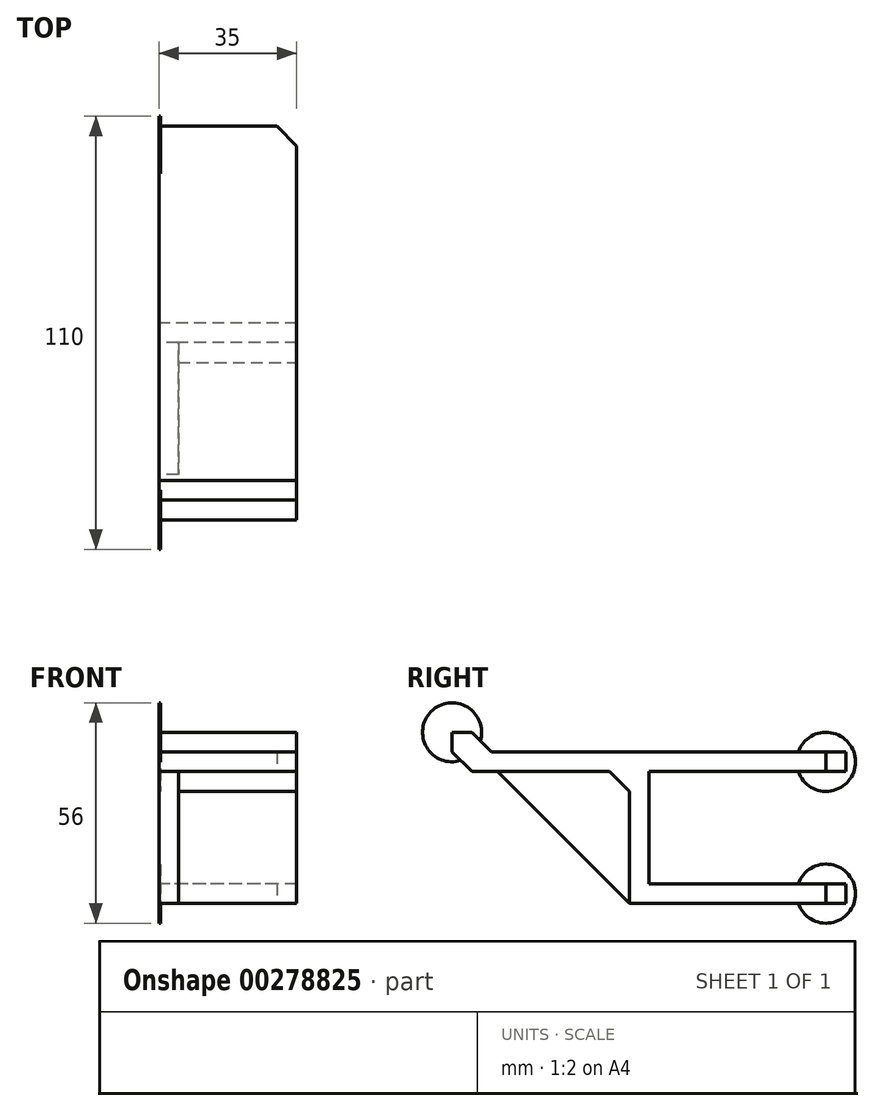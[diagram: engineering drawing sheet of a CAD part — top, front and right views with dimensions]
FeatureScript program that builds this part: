
annotation { "Feature Type Name" : "Feature", "Feature Type Description" : "" }
export const myFeature = defineFeature(function(context is Context, id is Id, definition is map)
    precondition{}
    {
        {
            var Q0;
            Q0=qCreatedBy(makeId("Right.planeOp"),FACE);
            var sketch = newSketch(context, id + "F0", { "sketchPlane" : qUnion([Q0])});
            skLineSegment(sketch, "E0.bottom", {"start": v(25, 14.25) * mm, "end": v(-25, 14.25) * mm});
            skLineSegment(sketch, "E0.top", {"start": v(25, -14.25) * mm, "end": v(-25, -14.25) * mm});
            skLineSegment(sketch, "E0.left", {"start": v(25, 14.25) * mm, "end": v(25, -14.25) * mm, "construction": true});
            skLineSegment(sketch, "E0.right", {"start": v(-25, 14.25) * mm, "end": v(-25, -14.25) * mm});
            skPoint(sketch, "E0.middle", {"position": v(0, 0) * mm});
            skLineSegment(sketch, "E1", {"start": v(25, 14.25) * mm, "end": v(25, 19.25) * mm});
            skLineSegment(sketch, "E2", {"start": v(25, 19.25) * mm, "end": v(-65, 19.25) * mm});
            skLineSegment(sketch, "E3", {"start": v(-65, 19.25) * mm, "end": v(-70, 24.25) * mm});
            skLineSegment(sketch, "E4", {"start": v(-70, 24.25) * mm, "end": v(-75, 24.25) * mm});
            skLineSegment(sketch, "E5", {"start": v(-30, -19.25) * mm, "end": v(25, -19.25) * mm});
            skLineSegment(sketch, "E6", {"start": v(25, -19.25) * mm, "end": v(25, -14.25) * mm});
            skLineSegment(sketch, "E7", {"start": v(-75, 24.25) * mm, "end": v(-75, 14.25) * mm});
            skLineSegment(sketch, "E8", {"start": v(-75, 14.25) * mm, "end": v(-30, 14.25) * mm});
            skLineSegment(sketch, "E9", {"start": v(-30, 14.25) * mm, "end": v(-30, -19.25) * mm});
            skLineSegment(sketch, "E10", {"start": v(-25, 14.25) * mm, "end": v(-30, 14.25) * mm, "construction": true});
            skSolve(sketch);
        }
        {
            var Q0;
            Q0=qSketchRegion(id+"F0",true);
            extrude(context, id + "F1", {"entities" : qUnion([Q0]), "endBound" : BoundingType.SYMMETRIC, "depth" : 35 * mm});
        }
        {
            var Q0;
            Q0=makeQuery(id+"F1.opExtrude","CAP_FACE",FACE,{"disambiguationData":[OSD([sQuery(id+"F0.wireOp",EDGE,"E0.bottom"),sQuery(id+"F0.wireOp",EDGE,"E0.top"),sQuery(id+"F0.wireOp",EDGE,"E0.right"),sQuery(id+"F0.wireOp",EDGE,"E1"),sQuery(id+"F0.wireOp",EDGE,"E2"),sQuery(id+"F0.wireOp",EDGE,"E3"),sQuery(id+"F0.wireOp",EDGE,"E4"),sQuery(id+"F0.wireOp",EDGE,"E5"),sQuery(id+"F0.wireOp",EDGE,"E6"),sQuery(id+"F0.wireOp",EDGE,"E7"),sQuery(id+"F0.wireOp",EDGE,"E8"),sQuery(id+"F0.wireOp",EDGE,"E9")])],"isStart":true});
            var sketch = newSketch(context, id + "F2", { "sketchPlane" : qUnion([Q0])});
            skLineSegment(sketch, "E11", {"start": v(30, -19.25) * mm, "end": v(63.5, 14.25) * mm});
            skLineSegment(sketch, "E12.0", {"start": v(30, 14.25) * mm, "end": v(30, -19.25) * mm});
            skLineSegment(sketch, "E13", {"start": v(30, 14.25) * mm, "end": v(63.5, 14.25) * mm});
            skSolve(sketch);
        }
        {
            var Q0;
            Q0=qSketchRegion(id+"F2",true);
            extrude(context, id + "F3", {"entities" : qUnion([Q0]), "operationType" : NewBodyOperationType.ADD, "oppositeDirection" : true, "depth" : 5 * mm});
        }
        {
            var Q0;
            Q0=makeQuery(id+"F1.opExtrude","CAP_EDGE",EDGE,{"disambiguationData":[OSD([sQuery(id+"F0.wireOp",EDGE,"E1")])],"isStart":false});
            var Q1;
            Q1=makeQuery(id+"F1.opExtrude","CAP_EDGE",EDGE,{"disambiguationData":[OSD([sQuery(id+"F0.wireOp",EDGE,"E1")])],"isStart":true});
            var Q2;
            Q2=makeQuery(id+"F1.opExtrude","CAP_EDGE",EDGE,{"disambiguationData":[OSD([sQuery(id+"F0.wireOp",EDGE,"E6")])],"isStart":false});
            var Q3;
            Q3=makeQuery(id+"F1.opExtrude","CAP_EDGE",EDGE,{"disambiguationData":[OSD([sQuery(id+"F0.wireOp",EDGE,"E6")])],"isStart":true});
            var Q4;
            Q4=makeQuery(id+"F1.opExtrude","SWEPT_EDGE",EDGE,{"disambiguationData":[OSD([sQuery(id+"F0.wireOp",EDGE,"E8"),sQuery(id+"F0.wireOp",EDGE,"E9")])]});
            var Q5;
            Q5=makeQuery(id+"F1.opExtrude","SWEPT_EDGE",EDGE,{"disambiguationData":[OSD([sQuery(id+"F0.wireOp",EDGE,"E7"),sQuery(id+"F0.wireOp",EDGE,"E8")])]});
            chamfer(context, id + "F4", {"entities" : qUnion([Q0, Q1, Q2, Q3, Q4, Q5]), "width" : 5 * mm, "tangentPropagation" : true});
        }
        {
            var Q0;
            Q0=makeQuery(id+"F3.boolean.opBoolean","MERGE",FACE,{"derivedFrom":[makeQuery(id+"F1.opExtrude","CAP_FACE",FACE,{"disambiguationData":[OSD([sQuery(id+"F0.wireOp",EDGE,"E0.bottom"),sQuery(id+"F0.wireOp",EDGE,"E0.top"),sQuery(id+"F0.wireOp",EDGE,"E0.right"),sQuery(id+"F0.wireOp",EDGE,"E1"),sQuery(id+"F0.wireOp",EDGE,"E2"),sQuery(id+"F0.wireOp",EDGE,"E3"),sQuery(id+"F0.wireOp",EDGE,"E4"),sQuery(id+"F0.wireOp",EDGE,"E5"),sQuery(id+"F0.wireOp",EDGE,"E6"),sQuery(id+"F0.wireOp",EDGE,"E7"),sQuery(id+"F0.wireOp",EDGE,"E8"),sQuery(id+"F0.wireOp",EDGE,"E9")])],"isStart":true}),makeQuery(id+"F3.opExtrude","CAP_FACE",FACE,{"disambiguationData":[OSD([sQuery(id+"F2.wireOp",EDGE,"E11"),sQuery(id+"F2.wireOp",EDGE,"E12.0"),sQuery(id+"F2.wireOp",EDGE,"E13")])],"isStart":true})]});
            var sketch = newSketch(context, id + "F5", { "sketchPlane" : qUnion([Q0])});
            skCircle(sketch, "E14", {"center": v(-20, -16.75) * mm, "radius": 7.5 * mm});
            skCircle(sketch, "E15", {"center": v(-20, 16.75) * mm, "radius": 7.5 * mm});
            skCircle(sketch, "E16", {"center": v(75, 24.25) * mm, "radius": 7.5 * mm});
            skSolve(sketch);
        }
        {
            var Q0;
            Q0=qSketchRegion(id+"F5",true);
            extrude(context, id + "F6", {"entities" : qUnion([Q0]), "operationType" : NewBodyOperationType.ADD, "oppositeDirection" : true, "depth" : 0.5 * mm});
        }
    });
